# Revit family: BIMLIB_ОтливПростой_GRANDLINE
name_source: partatom
category: Обобщенные модели
revit_build: Autodesk Revit 2017 (Build: 20170118_1100(x64)
units: mm (PartAtom-declared; Revit-internal decimal feet)

## family parameters
Может служить основой для арматурных стержней = Нет
Общий = Нет
При загрузке вырезать с полостями = Нет
Размер круглого соединителя = Использовать диаметр
Тип детали = Нормальный
Точка расчета площади = Нет

## types (5) — shared parameters
ADSK_URL документации изделия = https://www.grandline.ru
ADSK_URL страницы изделия = https://www.grandline.ru
ADSK_Версия Revit = 2017
ADSK_Группирование = Доборные элементы
ADSK_Единица измерения = м
ADSK_Завод-изготовитель = Grand Line
ADSK_Материал = GL_Drap_RAL7016
ADSK_Материал тип подсчета = 1
ADSK_Обозначение = ГОСТ 19904-90, ГОСТ 14918-80
BL_BIM library = https://bimlib.pro
URL = https://www.grandline.ru
Изготовитель = Grand Line

## per-type parameters (varying)
| type | ADSK_Код изделия | ADSK_Наименование | ADSK_Размер_Глубина | Описание |
| 50мм | M22.066.01 | Отлив 50 | 50 мм | Отлив 50 |
| 100мм | M22.066.02 | Отлив 100 | 100 мм | Отлив 100 |
| 150мм | M22.066.03 | Отлив 150 | 150 мм | Отлив 150 |
| 200мм | M22.066.04 | Отлив 200 | 200 мм | Отлив 200 |
| 250мм | M22.066.05 | Отлив 250 | 250 мм | Отлив 250 |
